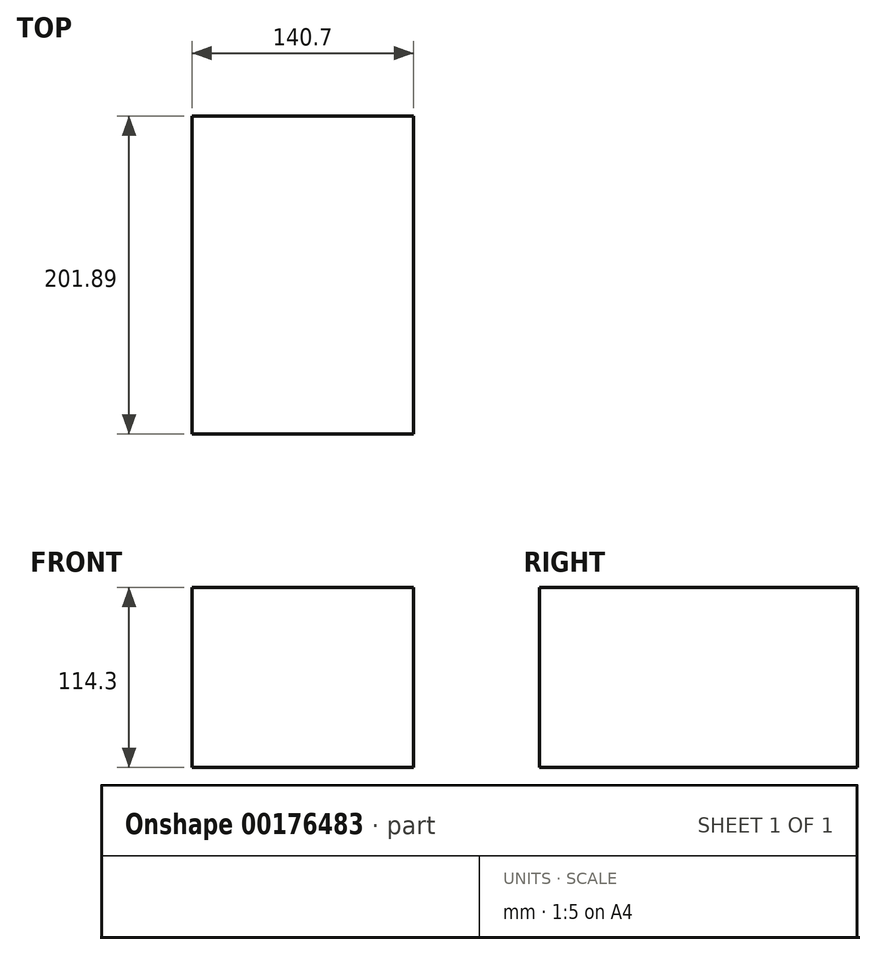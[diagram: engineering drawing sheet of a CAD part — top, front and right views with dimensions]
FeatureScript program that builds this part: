
annotation { "Feature Type Name" : "Feature", "Feature Type Description" : "" }
export const myFeature = defineFeature(function(context is Context, id is Id, definition is map)
    precondition{}
    {
        {
            var Q0;
            Q0=qCreatedBy(makeId("Top.planeOp"),FACE);
            var sketch = newSketch(context, id + "F0", { "sketchPlane" : qUnion([Q0])});
            skLineSegment(sketch, "E0.bottom", {"start": v(0, 0) * mm, "end": v(140.7, 0) * mm});
            skLineSegment(sketch, "E0.top", {"start": v(0, -201.9) * mm, "end": v(140.7, -201.9) * mm});
            skLineSegment(sketch, "E0.left", {"start": v(0, 0) * mm, "end": v(0, -201.9) * mm});
            skLineSegment(sketch, "E0.right", {"start": v(140.7, 0) * mm, "end": v(140.7, -201.9) * mm});
            skSolve(sketch);
        }
        {
            var Q0;
            Q0=makeQuery(id+"F0.imprint","IMPRINT",FACE,{"disambiguationData":[TD([[makeQuery(id+"F0.imprint","IMPRINT",EDGE,{"derivedFrom":sQuery(id+"F0.wireOp",EDGE,"E0.bottom")}),-1.0]])]});
            extrude(context, id + "F1", {"entities" : qUnion([Q0]), "depth" : 114.3 * mm});
        }
    });
